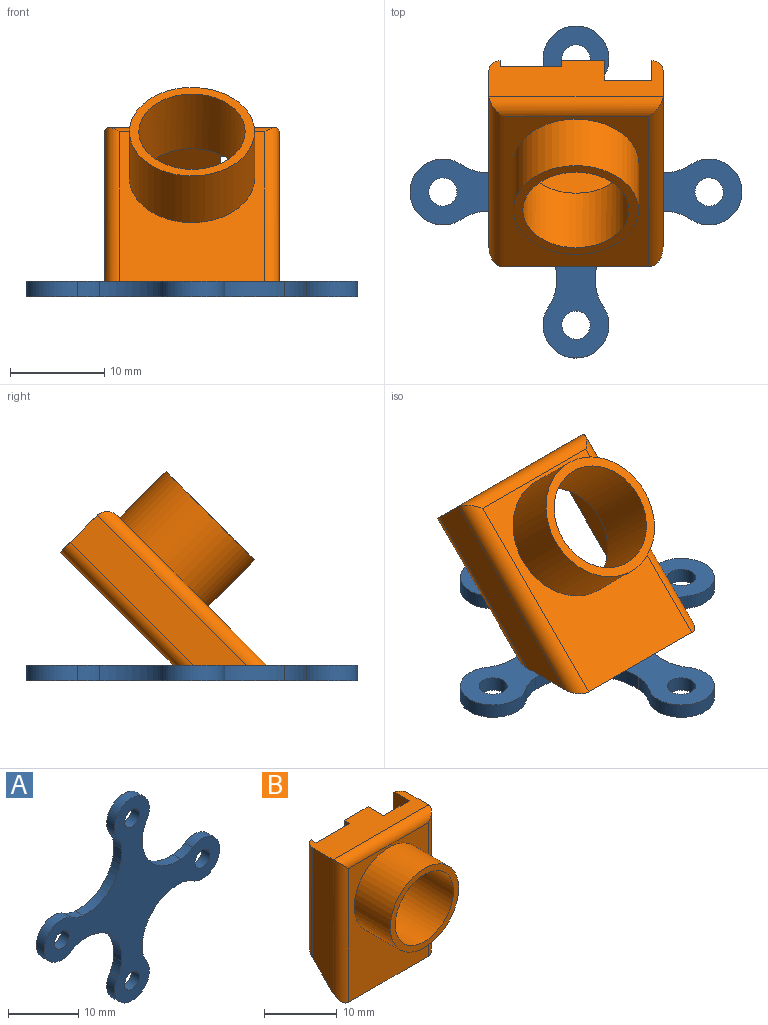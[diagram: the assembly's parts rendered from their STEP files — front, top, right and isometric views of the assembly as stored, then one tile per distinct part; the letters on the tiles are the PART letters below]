
ASSEMBLY  parts=2 mates=1
PART A: 22 faces, bbox 35.3x1.6x35.3 mm
  f0: cylinder r=5mm len=2.39mm, axis (0,1,0), area 4.1mm2, adj f1,f19,f20,f21
  f1: cylinder r=3.5mm len=7mm, axis (0,1,0), area 24.2mm2, adj f0,f2,f20,f21
  f2: cylinder r=5mm len=2.39mm, axis (0,1,0), area 4.1mm2, adj f1,f3,f20,f21
  f3: cylinder r=7.18mm len=7.75mm, axis (0,1,0), area 19.9mm2, adj f2,f4,f20,f21
  f4: cylinder r=5mm len=2.39mm, axis (0,1,0), area 4.1mm2, adj f3,f5,f20,f21
  f5: cylinder r=3.5mm len=7mm, axis (0,1,0), area 24.2mm2, adj f4,f6,f20,f21
  f6: cylinder r=5mm len=2.39mm, axis (0,1,0), area 4.1mm2, adj f5,f7,f20,f21
  f7: cylinder r=7.18mm len=7.75mm, axis (0,1,0), area 19.9mm2, adj f6,f8,f20,f21
  f8: cylinder r=5mm len=2.39mm, axis (0,1,0), area 4.1mm2, adj f7,f9,f20,f21
  f9: cylinder r=3.5mm len=7mm, axis (0,1,0), area 24.2mm2, adj f8,f10,f20,f21
  f10: cylinder r=5mm len=2.39mm, axis (0,1,0), area 4.1mm2, adj f9,f11,f20,f21
  f11: cylinder r=7.18mm len=7.75mm, axis (0,1,0), area 19.9mm2, adj f10,f12,f20,f21
  f12: cylinder r=5mm len=2.39mm, axis (0,1,0), area 4.1mm2, adj f11,f13,f20,f21
  f13: cylinder r=3.5mm len=7mm, axis (0,1,0), area 24.2mm2, adj f12,f14,f20,f21
  f14: cylinder r=5mm len=2.39mm, axis (0,1,0), area 4.1mm2, adj f13,f19,f20,f21
  f15: cylinder r=1.5mm len=3mm, axis (0,1,0), area 15.1mm2, adj f20,f21
  f16: cylinder r=1.5mm len=3mm, axis (0,1,0), area 15.1mm2, adj f20,f21
  f17: cylinder r=1.5mm len=3mm, axis (0,1,0), area 15.1mm2, adj f20,f21
  f18: cylinder r=1.5mm len=3mm, axis (0,1,0), area 15.1mm2, adj f20,f21
  f19: cylinder r=7.18mm len=7.75mm, axis (0,1,0), area 19.9mm2, adj f0,f14,f20,f21
  f20: plane 35.28x35.28mm, normal (0,-1,0), area 333.8mm2, adj f0,f1,f2,f3,f4,f5,f6,f7
  f21: plane 35.28x35.28mm, normal (0,1,0), area 333.8mm2, adj f0,f1,f2,f3,f4,f5,f6,f7
PART B: 24 faces, bbox 18.5x14x24 mm
  f0: plane 15.5x1.2mm, normal (0,1,0), area 18.6mm2, adj f7,f18,f19,f20
  f1: plane 22.5x4mm, normal (-1,0,0), area 82mm2, adj f2,f18,f20,f22
  f2: plane 18.5x5.5mm, normal (0,0,1), area 79.3mm2, adj f1,f4,f5,f8,f9,f14,f15,f16
  f3: plane 16.1x5.8mm, normal (0,0,-1), area 71.9mm2, adj f4,f8,f9,f10,f14,f15,f16,f17
  f4: plane 4.6x1.2mm, normal (0,1,0), area 5.5mm2, adj f2,f3,f14,f16
  f5: plane 22.5x4mm, normal (1,0,0), area 82mm2, adj f2,f18,f19,f21
  f6: plane 22.5x15.5mm, normal (0,-1,0), area 209.8mm2, adj f12,f18,f21,f22,f23
  f7: plane 16.1x5.8mm, normal (0,0,1), area 93.4mm2, adj f0,f8,f9,f10,f19,f20
  f8: plane 15.8x5.77mm, normal (-1,0,0), area 87.8mm2, adj f2,f3,f7,f10,f15,f19
  f9: plane 15.8x5.77mm, normal (1,0,0), area 85.4mm2, adj f2,f3,f7,f10,f17,f20
  f10: plane 16.1x14.6mm, normal (0,1,0), area 134.8mm2, adj f3,f7,f8,f9,f11
  f11: cylinder r=5.65mm len=11.3mm, axis (0,-1,0), area 291.1mm2, adj f10,f13
  f12: cylinder r=6.65mm len=13.3mm, axis (0,1,0), area 292.5mm2, adj f6,f13
  f13: plane 13.3x13.3mm, normal (0,-1,0), area 38.6mm2, adj f11,f12
  f14: plane 3x1.2mm, normal (1,0,0), area 3.6mm2, adj f2,f3,f4,f15
  f15: plane 5x1.2mm, normal (0,1,0), area 6mm2, adj f2,f3,f8,f14
  f16: plane 1.2x1mm, normal (-1,0,0), area 1.2mm2, adj f2,f3,f4,f17
  f17: plane 6.5x1.2mm, normal (0,1,0), area 7.8mm2, adj f2,f3,f9,f16
  f18: plane 18.5x7mm, normal (0,0.71,-0.71), area 180.4mm2, adj f0,f1,f5,f6,f19,f20,f21,f22
  f19: cylinder r=1.5mm len=18.5mm, axis (0,0,1), area 36.6mm2, adj f0,f2,f5,f7,f8,f18
  f20: cylinder r=1.5mm len=18.5mm, axis (0,0,-1), area 36.6mm2, adj f0,f1,f2,f7,f9,f18
  f21: cylinder r=1.5mm len=24mm, axis (0,0,-1), area 54mm2, adj f5,f6,f18,f23
  f22: cylinder r=1.5mm len=24mm, axis (0,0,1), area 54mm2, adj f1,f6,f18,f23
  f23: cylinder r=1.5mm len=18.5mm, axis (1,0,0), area 41mm2, adj f2,f6,f21,f22
PLACE A rot(axis=(1,0,0),90deg) t=(0,-29.72,-0.5)mm
PLACE B rot(axis=(-1,0,0),45deg) t=(0,-21.76,5.51)mm
MATE fastened B.f18 <-> A.f21  axis (0,0,-1) through (0,-32.72,-0.5)mm
